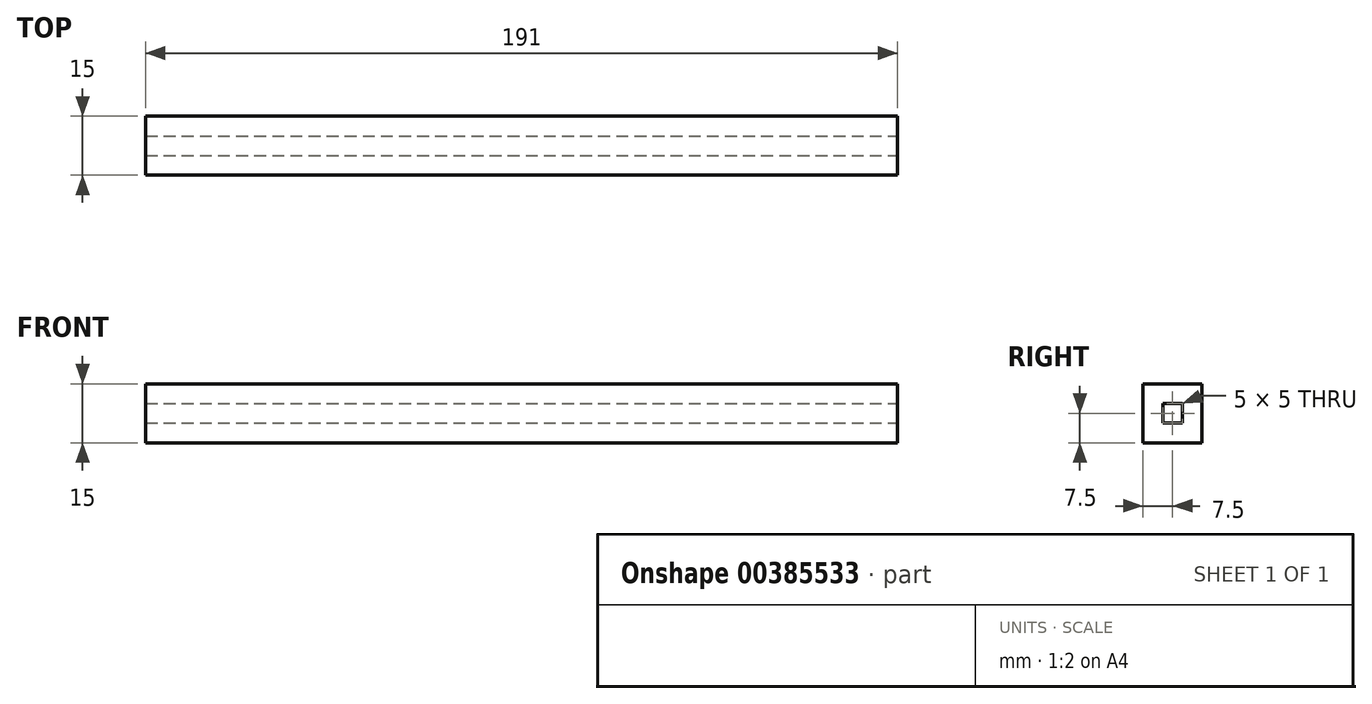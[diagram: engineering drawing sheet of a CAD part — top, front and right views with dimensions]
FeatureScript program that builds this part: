
annotation { "Feature Type Name" : "Feature", "Feature Type Description" : "" }
export const myFeature = defineFeature(function(context is Context, id is Id, definition is map)
    precondition{}
    {
        {
            var Q0;
            Q0=qCreatedBy(makeId("Front.planeOp"),FACE);
            var sketch = newSketch(context, id + "F0", { "sketchPlane" : qUnion([Q0])});
            skLineSegment(sketch, "E0.bottom", {"start": v(0, 0) * mm, "end": v(-191, 0) * mm});
            skLineSegment(sketch, "E0.top", {"start": v(0, 15) * mm, "end": v(-191, 15) * mm});
            skLineSegment(sketch, "E0.left", {"start": v(0, 0) * mm, "end": v(0, 15) * mm});
            skLineSegment(sketch, "E0.right", {"start": v(-191, 0) * mm, "end": v(-191, 15) * mm});
            skSolve(sketch);
        }
        {
            var Q0;
            Q0=makeQuery(id+"F0.imprint","IMPRINT",FACE,{"disambiguationData":[TD([[makeQuery(id+"F0.imprint","IMPRINT",EDGE,{"derivedFrom":sQuery(id+"F0.wireOp",EDGE,"E0.bottom")}),-1.0]])]});
            extrude(context, id + "F1", {"entities" : qUnion([Q0]), "depth" : 15 * mm});
        }
        {
            var Q0;
            Q0=makeQuery(id+"F1.opExtrude","SWEPT_FACE",FACE,{"disambiguationData":[OSD([sQuery(id+"F0.wireOp",EDGE,"E0.left")])]});
            var sketch = newSketch(context, id + "F2", { "sketchPlane" : qUnion([Q0])});
            skLineSegment(sketch, "E1.0", {"start": v(-5, 5) * mm, "end": v(-5, 10) * mm});
            skLineSegment(sketch, "E1.1", {"start": v(-10, 5) * mm, "end": v(-5, 5) * mm});
            skLineSegment(sketch, "E1.2", {"start": v(-10, 10) * mm, "end": v(-10, 5) * mm});
            skLineSegment(sketch, "E1.3", {"start": v(-5, 10) * mm, "end": v(-10, 10) * mm});
            skSolve(sketch);
        }
        {
            var Q0;
            Q0=makeQuery(id+"F2.imprint","IMPRINT",FACE,{"disambiguationData":[TD([[makeQuery(id+"F2.imprint","IMPRINT",EDGE,{"derivedFrom":sQuery(id+"F2.wireOp",EDGE,"E1.0")}),1.0]])]});
            extrude(context, id + "F3", {"entities" : qUnion([Q0]), "operationType" : NewBodyOperationType.REMOVE, "oppositeDirection" : true, "depth" : 200 * mm});
        }
    });
